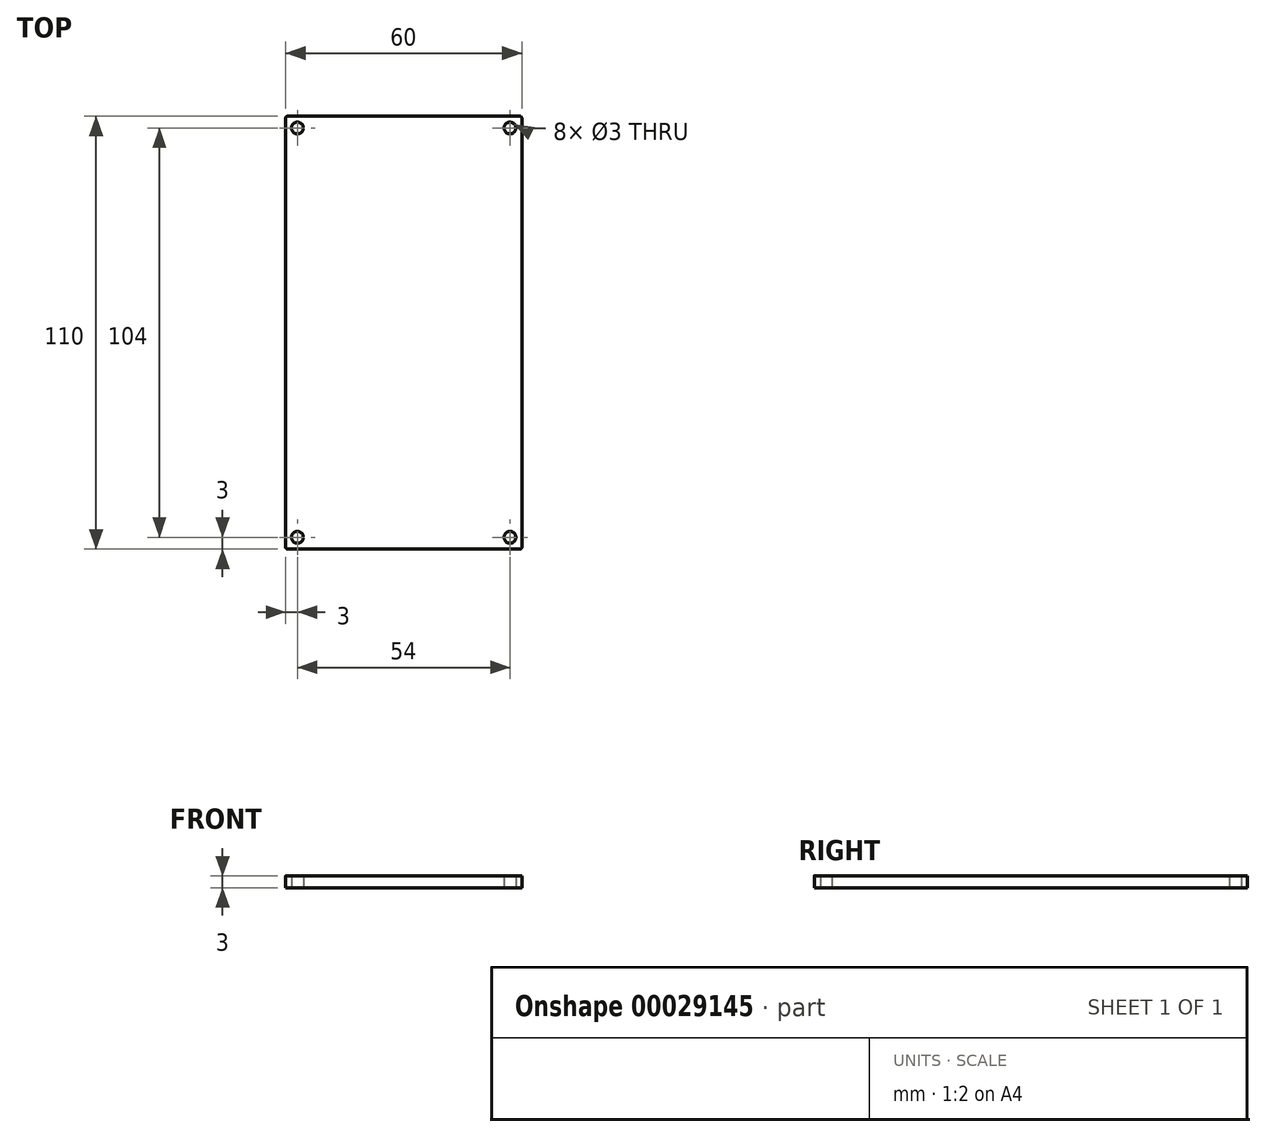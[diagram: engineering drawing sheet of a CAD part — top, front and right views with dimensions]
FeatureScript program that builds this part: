
annotation { "Feature Type Name" : "Feature", "Feature Type Description" : "" }
export const myFeature = defineFeature(function(context is Context, id is Id, definition is map)
    precondition{}
    {
        {
            var Q0;
            Q0=qCreatedBy(makeId("Top.planeOp"),FACE);
            var sketch = newSketch(context, id + "F0", { "sketchPlane" : qUnion([Q0])});
            skLineSegment(sketch, "E0.rect.bottom", {"start": v(29.5, -55) * mm, "end": v(-29.5, -55) * mm});
            skLineSegment(sketch, "E0.rect.top", {"start": v(29.5, 55) * mm, "end": v(-29.5, 55) * mm});
            skLineSegment(sketch, "E0.rect.left", {"start": v(30, -54.5) * mm, "end": v(30, 54.5) * mm});
            skLineSegment(sketch, "E0.rect.right", {"start": v(-30, -54.5) * mm, "end": v(-30, 54.5) * mm});
            skCircle(sketch, "E1", {"center": v(-27, 52) * mm, "radius": 1.5 * mm});
            skLineSegment(sketch, "E2", {"start": v(30.94, 1.26) * mm, "end": v(30, 0) * mm, "construction": true});
            skCircle(sketch, "E3.MirrorC", {"center": v(-27, -52) * mm, "radius": 1.5 * mm});
            skCircle(sketch, "E4.MirrorC", {"center": v(27, -52) * mm, "radius": 1.5 * mm});
            skCircle(sketch, "E5.MirrorC", {"center": v(27, 52) * mm, "radius": 1.5 * mm});
            skPoint(sketch, "E6.visualSharp", {"position": v(-30, 55) * mm});
            skArc(sketch, "E6.filletArc", {"start": v(-29.5, 55) * mm, "mid": v(-29.85, 54.85) * mm, "end": v(-30, 54.5) * mm});
            skPoint(sketch, "E7.visualSharp", {"position": v(30, 55) * mm});
            skArc(sketch, "E7.filletArc", {"start": v(30, 54.5) * mm, "mid": v(29.85, 54.85) * mm, "end": v(29.5, 55) * mm});
            skPoint(sketch, "E8.visualSharp", {"position": v(30, -55) * mm});
            skArc(sketch, "E8.filletArc", {"start": v(29.5, -55) * mm, "mid": v(29.85, -54.85) * mm, "end": v(30, -54.5) * mm});
            skPoint(sketch, "E9.visualSharp", {"position": v(-30, -55) * mm});
            skArc(sketch, "E9.filletArc", {"start": v(-30, -54.5) * mm, "mid": v(-29.85, -54.85) * mm, "end": v(-29.5, -55) * mm});
            skSolve(sketch);
        }
        {
            var Q0;
            Q0=makeQuery(id+"F0.imprint","IMPRINT",FACE,{"disambiguationData":[TD([[makeQuery(id+"F0.imprint","IMPRINT",EDGE,{"derivedFrom":sQuery(id+"F0.wireOp",EDGE,"E0.rect.bottom")}),-1.0]])]});
            extrude(context, id + "F1", {"entities" : qUnion([Q0]), "depth" : 3 * mm});
        }
    });
